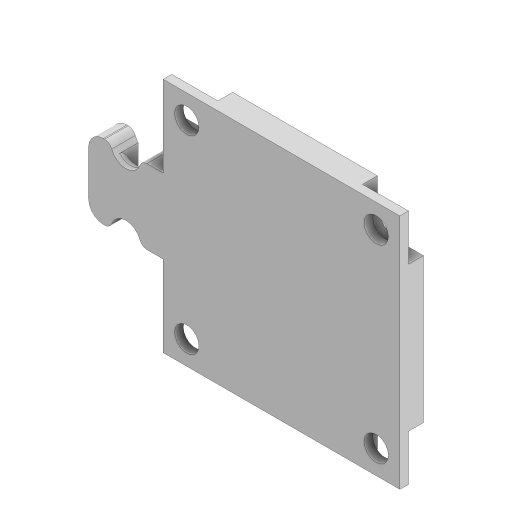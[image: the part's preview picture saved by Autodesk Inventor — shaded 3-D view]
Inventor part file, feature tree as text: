
AUTODESK INVENTOR PART (.ipt)
format: ipt  version: 2023 (Build 270158000, 158)  size: 194,560 bytes
history: native  units: mm
features: extrude x4, sketch x3, fillet x2
ambient origin geometry x8: Origin, YZ Plane, XZ Plane, XY Plane, X Axis, Y Axis, Z Axis, Center Point
bodies: Solid1 (feature_tree)
feature tree (9):
  extrude  "Extrusion1"  Depth=31.75mm
  sketch  "Sketch2"  dims[d3=3.15mm d4=0.0mm d5=3.2639mm]
  extrude  "Extrusion2"  Depth=3.15mm
  extrude  "Extrusion3"  Depth=2.0mm
  extrude  "Extrusion4"  Depth=2.0mm
  fillet  "Fillet1"  Radius=3.175mm
  fillet  "Fillet2"  Radius=3.175mm
  sketch  "Sketch1"  dims[d0=31.75mm d1=31.75mm]
  sketch  "Sketch3"  dims[d6=6.0mm d7=25.4mm d8=25.4mm d9=3.175mm d10=3.175mm d11=40.0mm d13=360.0deg d15=2.0mm d16=0.0mm d17=2.0mm d18=0.0mm d19=10.0mm d20=4.0mm d21=4.0mm d22=10.0mm d23=0.0mm d26=0.5mm d27=0.5mm d28=3.0mm d29=1.5mm d30=0.0mm d31=1.0mm d32=2.0mm]
